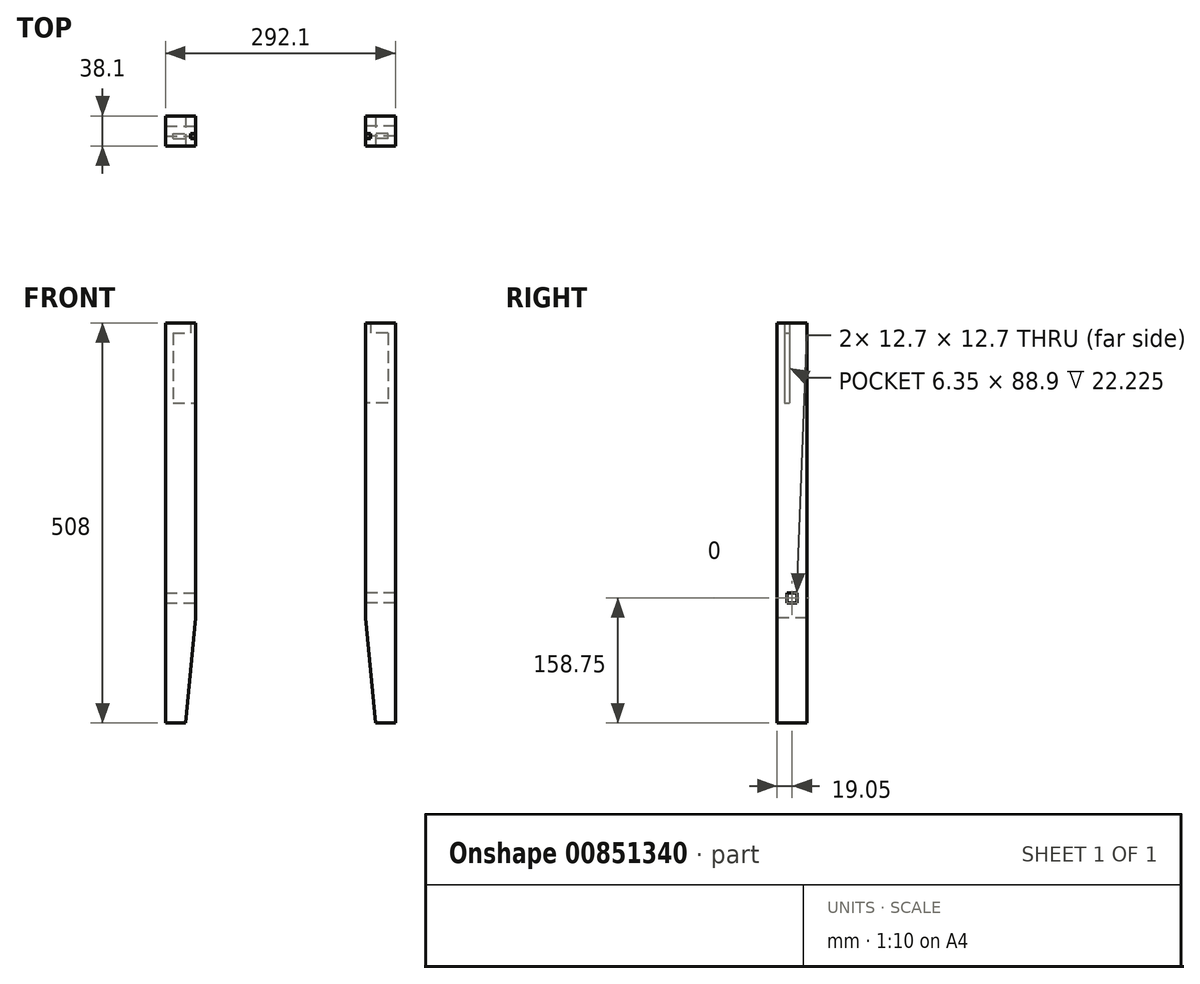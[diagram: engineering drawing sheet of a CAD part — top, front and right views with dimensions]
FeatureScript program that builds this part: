
annotation { "Feature Type Name" : "Feature", "Feature Type Description" : "" }
export const myFeature = defineFeature(function(context is Context, id is Id, definition is map)
    precondition{}
    {
        {
            var Q0;
            Q0=qCreatedBy(makeId("Right.planeOp"),FACE);
            var sketch = newSketch(context, id + "F0", { "sketchPlane" : qUnion([Q0])});
            skLineSegment(sketch, "E0", {"start": v(0, 46.62) * mm, "end": v(0, 24.2) * mm, "construction": true});
            skSolve(sketch);
        }
        {
            var Q0;
            Q0=qCreatedBy(makeId("Right.planeOp"),FACE);
            var Q1;
            Q1=sQuery(id+"F0.wireOp",EDGE,"E0");
            cPlane(context, id + "F1", {"entities" : qUnion([Q0, Q1]), "cplaneType" : CPlaneType.LINE_ANGLE, "offset" : 25.4 * mm, "angle" : 45 * degree, "width" : 152.4 * mm, "height" : 152.4 * mm});
        }
        {
            var Q0;
            Q0=qCreatedBy(makeId("Top.planeOp"),FACE);
            var sketch = newSketch(context, id + "F2", { "sketchPlane" : qUnion([Q0])});
            skLineSegment(sketch, "E1.bottom", {"start": v(-19.05, 19.05) * mm, "end": v(19.05, 19.05) * mm});
            skLineSegment(sketch, "E1.top", {"start": v(-19.05, -19.05) * mm, "end": v(19.05, -19.05) * mm});
            skLineSegment(sketch, "E1.left", {"start": v(-19.05, 19.05) * mm, "end": v(-19.05, -19.05) * mm});
            skLineSegment(sketch, "E1.right", {"start": v(19.05, 19.05) * mm, "end": v(19.05, -19.05) * mm});
            skLineSegment(sketch, "E2", {"start": v(-19.05, 19.05) * mm, "end": v(19.05, -19.05) * mm, "construction": true});
            skSolve(sketch);
        }
        {
            var Q0;
            Q0 = qSketchRegion(id + "F2", true);
            extrude(context, id + "F3", {"entities" : qUnion([Q0]), "oppositeDirection" : true, "depth" : 508 * mm, "offsetDistance" : 25.4 * mm});
        }
        {
            var Q0;
            Q0=makeQuery(id+"F3.opExtrude","SWEPT_FACE",FACE,{"disambiguationData":[OSD([sQuery(id+"F2.wireOp",EDGE,"E1.right")])]});
            var sketch = newSketch(context, id + "F4", { "sketchPlane" : qUnion([Q0])});
            skLineSegment(sketch, "E3", {"start": v(-19.05, -355.6) * mm, "end": v(19.05, -355.6) * mm, "construction": true});
            skLineSegment(sketch, "E4.bottom", {"start": v(-6.35, -342.9) * mm, "end": v(6.35, -342.9) * mm});
            skLineSegment(sketch, "E4.top", {"start": v(-6.35, -355.6) * mm, "end": v(6.35, -355.6) * mm});
            skLineSegment(sketch, "E4.left", {"start": v(-6.35, -342.9) * mm, "end": v(-6.35, -355.6) * mm});
            skLineSegment(sketch, "E4.right", {"start": v(6.35, -342.9) * mm, "end": v(6.35, -355.6) * mm});
            skLineSegment(sketch, "E5", {"start": v(0, -342.9) * mm, "end": v(0, -355.6) * mm, "construction": true});
            skLineSegment(sketch, "E6.bottom", {"start": v(-9.52, 0) * mm, "end": v(-3.17, 0) * mm});
            skLineSegment(sketch, "E6.top", {"start": v(-9.52, -101.6) * mm, "end": v(-3.17, -101.6) * mm});
            skLineSegment(sketch, "E6.left", {"start": v(-9.53, 0) * mm, "end": v(-9.52, -101.6) * mm});
            skLineSegment(sketch, "E6.right", {"start": v(-3.17, 0) * mm, "end": v(-3.17, -101.6) * mm});
            skLineSegment(sketch, "E7", {"start": v(-9.52, -12.7) * mm, "end": v(-3.17, -12.7) * mm});
            skSolve(sketch);
        }
        {
            var Q0;
            {var subQ0=sQuery(id+"F4.wireOp",EDGE,"E6.top");Q0=makeQuery(id+"F4.imprint","IMPRINT",FACE,{"disambiguationData":[TD([[makeQuery(id+"F4.imprint","IMPRINT",EDGE,{"derivedFrom":subQ0}),1.0]])]});}
            var Q1;
            Q1=makeQuery(id+"F3.opExtrude","SWEPT_FACE",FACE,{"disambiguationData":[OSD([sQuery(id+"F2.wireOp",EDGE,"E1.left")])]});
            extrude(context, id + "F5", {"entities" : qUnion([Q0]), "operationType" : NewBodyOperationType.REMOVE, "oppositeDirection" : true, "depth" : 28.57 * mm, "endBoundEntityFace" : qUnion([Q1]), "hasOffset" : true, "offsetDistance" : 12.7 * mm});
        }
        {
            var Q0;
            {var subQ0=sQuery(id+"F4.wireOp",EDGE,"E6.bottom");Q0=makeQuery(id+"F4.imprint","IMPRINT",FACE,{"disambiguationData":[TD([[makeQuery(id+"F4.imprint","IMPRINT",EDGE,{"derivedFrom":subQ0}),1.0]])]});}
            extrude(context, id + "F6", {"entities" : qUnion([Q0]), "operationType" : NewBodyOperationType.REMOVE, "oppositeDirection" : true, "depth" : 6.35 * mm, "offsetDistance" : 25.4 * mm});
        }
        {
            var Q0;
            Q0=makeQuery(id+"F4.imprint","IMPRINT",FACE,{"disambiguationData":[TD([[makeQuery(id+"F4.imprint","IMPRINT",EDGE,{"derivedFrom":sQuery(id+"F4.wireOp",EDGE,"E4.bottom")}),-1.0]])]});
            extrude(context, id + "F7", {"entities" : qUnion([Q0]), "operationType" : NewBodyOperationType.REMOVE, "endBound" : BoundingType.THROUGH_ALL, "oppositeDirection" : true, "depth" : 25.4 * mm, "offsetDistance" : 25.4 * mm});
        }
        {
            var Q0;
            Q0=makeQuery(id+"F3.opExtrude","SWEPT_FACE",FACE,{"disambiguationData":[OSD([sQuery(id+"F2.wireOp",EDGE,"E1.top")])]});
            var sketch = newSketch(context, id + "F8", { "sketchPlane" : qUnion([Q0])});
            skLineSegment(sketch, "E8", {"start": v(-19.05, -374.65) * mm, "end": v(19.05, -374.65) * mm, "construction": true});
            skLineSegment(sketch, "E9", {"start": v(19.05, -374.65) * mm, "end": v(6.35, -508) * mm});
            skLineSegment(sketch, "E10.0", {"start": v(6.35, -508) * mm, "end": v(19.05, -508) * mm});
            skLineSegment(sketch, "E11.0", {"start": v(19.05, -508) * mm, "end": v(19.05, -374.65) * mm});
            skPoint(sketch, "E12.orphan", {"position": v(19.05, 0) * mm});
            skSolve(sketch);
        }
        {
            var Q0;
            Q0 = qSketchRegion(id + "F8", true);
            extrude(context, id + "F9", {"entities" : qUnion([Q0]), "operationType" : NewBodyOperationType.REMOVE, "endBound" : BoundingType.THROUGH_ALL, "oppositeDirection" : true, "depth" : 25.4 * mm, "offsetDistance" : 25.4 * mm});
        }
        {
            var Q0;
            Q0=qCreatedBy(makeId("Right.planeOp"),FACE);
            cPlane(context, id + "F10", {"entities" : qUnion([Q0]), "cplaneType" : CPlaneType.OFFSET, "offset" : 127 * mm, "width" : 152.4 * mm, "height" : 152.4 * mm});
        }
        {
            var Q0;
            Q0=makeQuery(id+"F3.opExtrude","SWEPT_BODY",BODY,{"disambiguationData":[OSD([sQuery(id+"F2.wireOp",EDGE,"E1.bottom"),sQuery(id+"F2.wireOp",EDGE,"E1.top"),sQuery(id+"F2.wireOp",EDGE,"E1.left"),sQuery(id+"F2.wireOp",EDGE,"E1.right")])]});
            var Q1;
            Q1=qCreatedBy(id+"F10.planeOp",FACE);
            mirror(context, id + "F11", {"entities" : qUnion([Q0]), "mirrorPlane" : qUnion([Q1])});
        }
    });
